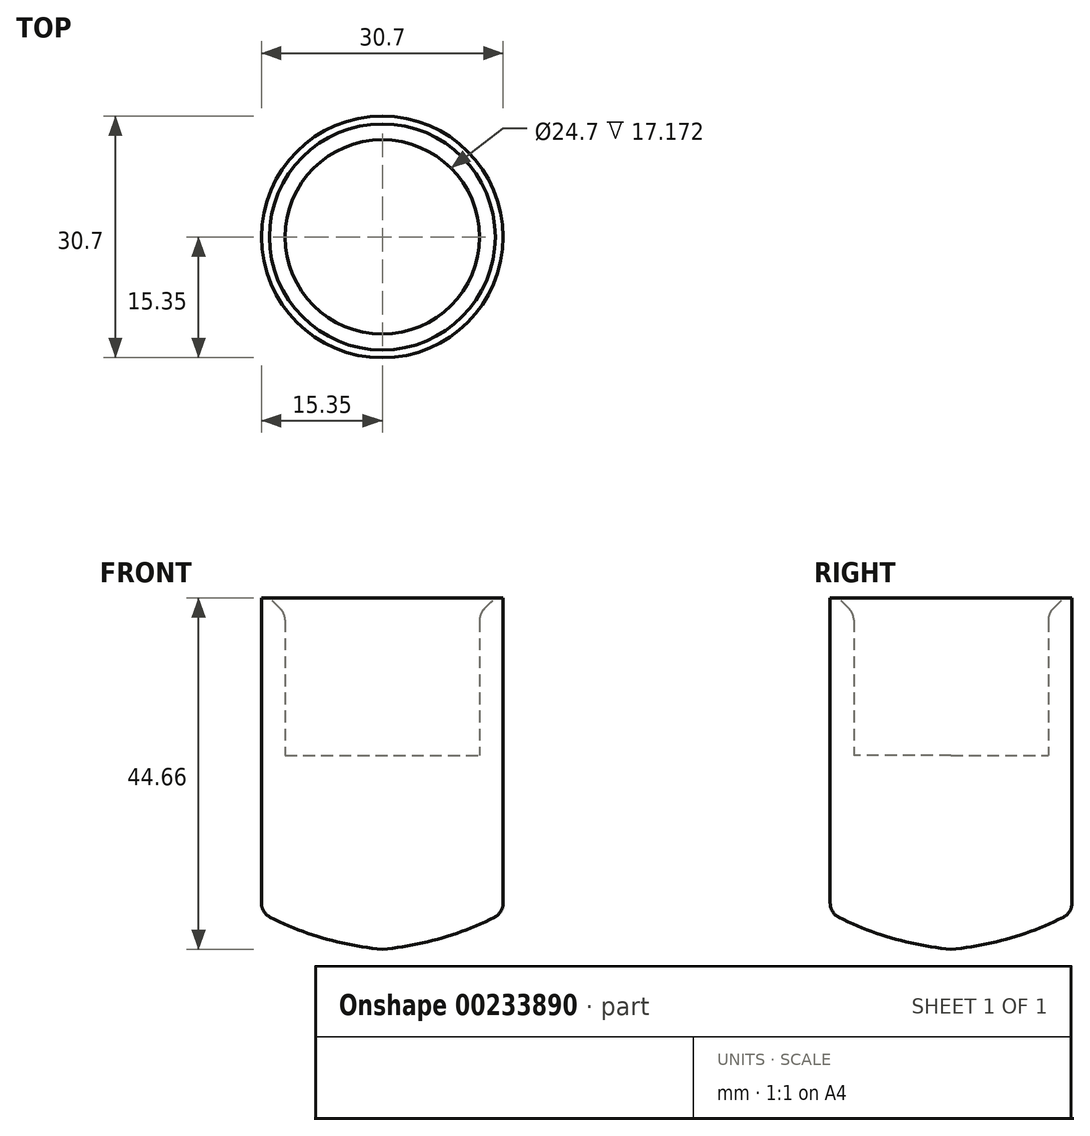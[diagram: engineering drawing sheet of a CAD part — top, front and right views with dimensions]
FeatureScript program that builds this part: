
annotation { "Feature Type Name" : "Feature", "Feature Type Description" : "" }
export const myFeature = defineFeature(function(context is Context, id is Id, definition is map)
    precondition{}
    {
        {
            var Q0;
            Q0=qCreatedBy(makeId("Top.planeOp"),FACE);
            var sketch = newSketch(context, id + "F0", { "sketchPlane" : qUnion([Q0])});
            skCircle(sketch, "E0", {"center": v(0, 0) * mm, "radius": 12.35 * mm});
            skCircle(sketch, "E1.0", {"center": v(0, 0) * mm, "radius": 15.35 * mm});
            skSolve(sketch);
        }
        {
            var Q0;
            Q0=makeQuery(id+"F0.imprint","IMPRINT",FACE,{"disambiguationData":[TD([[makeQuery(id+"F0.imprint","IMPRINT",EDGE,{"derivedFrom":sQuery(id+"F0.wireOp",EDGE,"E0")}),-1.0]])]});
            extrude(context, id + "F1", {"entities" : qUnion([Q0]), "depth" : 20 * mm});
        }
        {
            var Q0;
            Q0=qCreatedBy(makeId("Front.planeOp"),FACE);
            var sketch = newSketch(context, id + "F2", { "sketchPlane" : qUnion([Q0])});
            skLineSegment(sketch, "E2", {"start": v(-15.35, 0) * mm, "end": v(-15.35, -20) * mm});
            skLineSegment(sketch, "E3", {"start": v(-15.35, 0) * mm, "end": v(-15.35, 20) * mm, "construction": true});
            skArc(sketch, "E4", {"start": v(-15.35, -20) * mm, "mid": v(-7.91, -23.1) * mm, "end": v(0, -24.66) * mm});
            skLineSegment(sketch, "E5", {"start": v(0, -24.66) * mm, "end": v(0, 0) * mm});
            skLineSegment(sketch, "E6", {"start": v(0, 0) * mm, "end": v(-15.35, 0) * mm});
            skSolve(sketch);
        }
        {
            var Q0;
            Q0=makeQuery(id+"F2.imprint","IMPRINT",FACE,{"disambiguationData":[TD([[makeQuery(id+"F2.imprint","IMPRINT",EDGE,{"derivedFrom":sQuery(id+"F2.wireOp",EDGE,"E2")}),1.0]])]});
            var Q1;
            Q1=sQuery(id+"F2.wireOp",EDGE,"E5");
            revolve(context, id + "F3", {"operationType" : NewBodyOperationType.ADD, "entities" : qUnion([Q0]), "axis" : qUnion([Q1]), "revolveType" : RevolveType.FULL});
        }
        {
            var Q0;
            Q0=makeQuery(id+"F3.opRevolve","SWEPT_EDGE",EDGE,{"disambiguationData":[OSD([sQuery(id+"F2.wireOp",EDGE,"E2"),sQuery(id+"F2.wireOp",EDGE,"E4")])]});
            fillet(context, id + "F4", {"entities" : qUnion([Q0]), "radius" : 2 * mm, "tangentPropagation" : true, "allowEdgeOverflow" : false});
        }
        {
            var Q0;
            Q0=makeQuery(id+"F1.opExtrude","CAP_EDGE",EDGE,{"disambiguationData":[OSD([sQuery(id+"F0.wireOp",EDGE,"E0")])],"isStart":false});
            chamfer(context, id + "F5", {"entities" : qUnion([Q0]), "width" : 2 * mm, "tangentPropagation" : true});
        }
        {
            var Q0;
            {var subQ0=sQuery(id+"F0.wireOp",EDGE,"E0");Q0=makeQuery(id+"F5.opChamfer","BLEND_EDGE",EDGE,{"blendedFrom":[makeQuery(id+"F1.opExtrude","CAP_EDGE",EDGE,{"disambiguationData":[OSD([subQ0])],"isStart":false}),makeQuery(id+"F1.opExtrude","SWEPT_FACE",FACE,{"disambiguationData":[OSD([subQ0])]})],"blendedInto":[makeQuery(id+"F1.opExtrude","SWEPT_FACE",FACE,{"disambiguationData":[OSD([subQ0])]})]});}
            fillet(context, id + "F6", {"entities" : qUnion([Q0]), "radius" : 2 * mm, "tangentPropagation" : true, "allowEdgeOverflow" : false});
        }
    });
